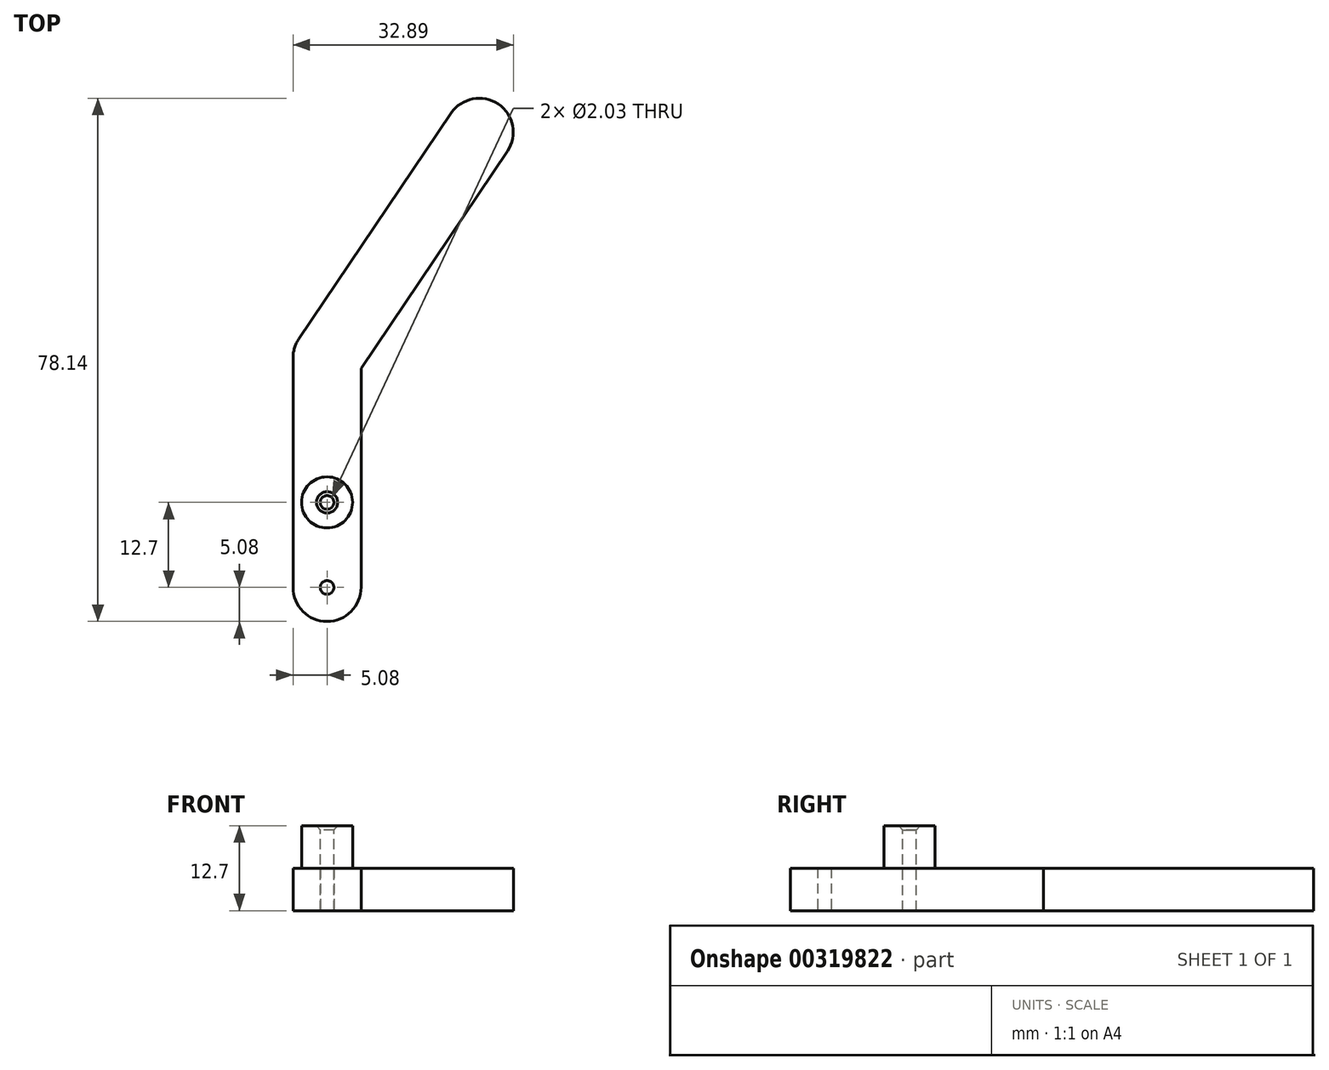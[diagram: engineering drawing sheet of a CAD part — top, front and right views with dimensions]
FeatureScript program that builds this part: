
annotation { "Feature Type Name" : "Feature", "Feature Type Description" : "" }
export const myFeature = defineFeature(function(context is Context, id is Id, definition is map)
    precondition{}
    {
        {
            var Q0;
            Q0=qCreatedBy(makeId("Top.planeOp"),FACE);
            var sketch = newSketch(context, id + "F0", { "sketchPlane" : qUnion([Q0])});
            skLineSegment(sketch, "E0", {"start": v(0, -21.59) * mm, "end": v(0, 0) * mm});
            skLineSegment(sketch, "E1", {"start": v(0, 0) * mm, "end": v(22.73, 33.7) * mm});
            skLineSegment(sketch, "E2", {"start": v(0, -34.3) * mm, "end": v(0, -21.59) * mm});
            skArc(sketch, "E3.0.startCap", {"start": v(4.21, -2.84) * mm, "mid": v(-2.84, -4.21) * mm, "end": v(-4.21, 2.84) * mm});
            skArc(sketch, "E3.0.endCap", {"start": v(18.51, 36.53) * mm, "mid": v(25.57, 37.9) * mm, "end": v(26.94, 30.85) * mm});
            skLineSegment(sketch, "E3.0.left", {"start": v(-4.21, 2.84) * mm, "end": v(18.51, 36.53) * mm});
            skLineSegment(sketch, "E3.0.right", {"start": v(4.21, -2.84) * mm, "end": v(26.94, 30.85) * mm});
            skArc(sketch, "E3.1.startCap", {"start": v(5.08, -34.3) * mm, "mid": v(0, -39.37) * mm, "end": v(-5.08, -34.3) * mm});
            skArc(sketch, "E3.1.endCap", {"start": v(-5.08, -21.59) * mm, "mid": v(0, -16.51) * mm, "end": v(5.08, -21.59) * mm});
            skLineSegment(sketch, "E3.1.left", {"start": v(-5.08, -34.3) * mm, "end": v(-5.08, -21.59) * mm});
            skLineSegment(sketch, "E3.1.right", {"start": v(5.08, -34.3) * mm, "end": v(5.08, -21.59) * mm});
            skArc(sketch, "E3.2.startCap", {"start": v(5.08, -21.59) * mm, "mid": v(0, -26.67) * mm, "end": v(-5.08, -21.59) * mm});
            skArc(sketch, "E3.2.endCap", {"start": v(-5.08, 0) * mm, "mid": v(0, 5.08) * mm, "end": v(5.08, 0) * mm});
            skLineSegment(sketch, "E3.2.left", {"start": v(-5.08, -21.59) * mm, "end": v(-5.08, 0) * mm});
            skLineSegment(sketch, "E3.2.right", {"start": v(5.08, -21.59) * mm, "end": v(5.08, 0) * mm});
            skSolve(sketch);
        }
        {
            var Q0;
            Q0 = qSketchRegion(id + "F0", true);
            extrude(context, id + "F1", {"entities" : qUnion([Q0]), "depth" : 6.35 * mm});
        }
        {
            var Q0;
            Q0=makeQuery(id+"F1.opExtrude","CAP_FACE",FACE,{"disambiguationData":[OSD([sQuery(id+"F0.wireOp",EDGE,"E3.0.endCap"),sQuery(id+"F0.wireOp",EDGE,"E3.0.left"),sQuery(id+"F0.wireOp",EDGE,"E3.0.right"),sQuery(id+"F0.wireOp",EDGE,"E3.1.startCap"),sQuery(id+"F0.wireOp",EDGE,"E3.1.left"),sQuery(id+"F0.wireOp",EDGE,"E3.1.right"),sQuery(id+"F0.wireOp",EDGE,"E3.2.endCap"),sQuery(id+"F0.wireOp",EDGE,"E3.2.left"),sQuery(id+"F0.wireOp",EDGE,"E3.2.right")])],"isStart":false});
            var sketch = newSketch(context, id + "F2", { "sketchPlane" : qUnion([Q0])});
            skCircle(sketch, "E4", {"center": v(0, -21.59) * mm, "radius": 3.81 * mm});
            skSolve(sketch);
        }
        {
            var Q0;
            Q0 = qSketchRegion(id + "F2", true);
            extrude(context, id + "F3", {"entities" : qUnion([Q0]), "operationType" : NewBodyOperationType.ADD, "depth" : 6.35 * mm});
        }
        {
            var Q0;
            Q0=makeQuery(id+"F3.opExtrude","CAP_FACE",FACE,{"disambiguationData":[OSD([sQuery(id+"F2.wireOp",EDGE,"E4")])],"isStart":false});
            var sketch = newSketch(context, id + "F4", { "sketchPlane" : qUnion([Q0])});
            skPoint(sketch, "E5", {"position": v(0, -21.59) * mm});
            skSolve(sketch);
        }
        {
            var Q0;
            Q0=sQuery(id+"F4.wireOp",VERTEX,"E5");
            var Q1;
            Q1=makeQuery(id+"F1.opExtrude","SWEPT_BODY",BODY,{"disambiguationData":[OSD([sQuery(id+"F0.wireOp",EDGE,"E3.0.endCap"),sQuery(id+"F0.wireOp",EDGE,"E3.0.left"),sQuery(id+"F0.wireOp",EDGE,"E3.0.right"),sQuery(id+"F0.wireOp",EDGE,"E3.1.startCap"),sQuery(id+"F0.wireOp",EDGE,"E3.1.left"),sQuery(id+"F0.wireOp",EDGE,"E3.1.right"),sQuery(id+"F0.wireOp",EDGE,"E3.2.endCap"),sQuery(id+"F0.wireOp",EDGE,"E3.2.left"),sQuery(id+"F0.wireOp",EDGE,"E3.2.right")])]});
            hole(context, id + "F5", {"style" : HoleStyle.C_SINK, "endStyle" : HoleEndStyle.THROUGH, "holeDiameter" : 2.03 * mm, "cSinkDiameter" : 3.17 * mm, "cSinkAngle" : 82 * degree, "tappedDepth" : 12.7 * mm, "tapClearance" : 3, "locations" : qUnion([Q0]), "scope" : qUnion([Q1])});
        }
        {
            var Q0;
            Q0=sQuery(id+"F0.wireOp",VERTEX,"E3.1.startCap.center");
            var Q1;
            Q1=makeQuery(id+"F1.opExtrude","SWEPT_BODY",BODY,{"disambiguationData":[OSD([sQuery(id+"F0.wireOp",EDGE,"E3.0.endCap"),sQuery(id+"F0.wireOp",EDGE,"E3.0.left"),sQuery(id+"F0.wireOp",EDGE,"E3.0.right"),sQuery(id+"F0.wireOp",EDGE,"E3.1.startCap"),sQuery(id+"F0.wireOp",EDGE,"E3.1.left"),sQuery(id+"F0.wireOp",EDGE,"E3.1.right"),sQuery(id+"F0.wireOp",EDGE,"E3.2.endCap"),sQuery(id+"F0.wireOp",EDGE,"E3.2.left"),sQuery(id+"F0.wireOp",EDGE,"E3.2.right")])]});
            hole(context, id + "F6", {"style" : HoleStyle.SIMPLE, "endStyle" : HoleEndStyle.THROUGH, "oppositeDirection" : true, "holeDiameter" : 2.03 * mm, "tappedDepth" : 12.7 * mm, "tapClearance" : 3, "locations" : qUnion([Q0]), "scope" : qUnion([Q1])});
        }
    });
